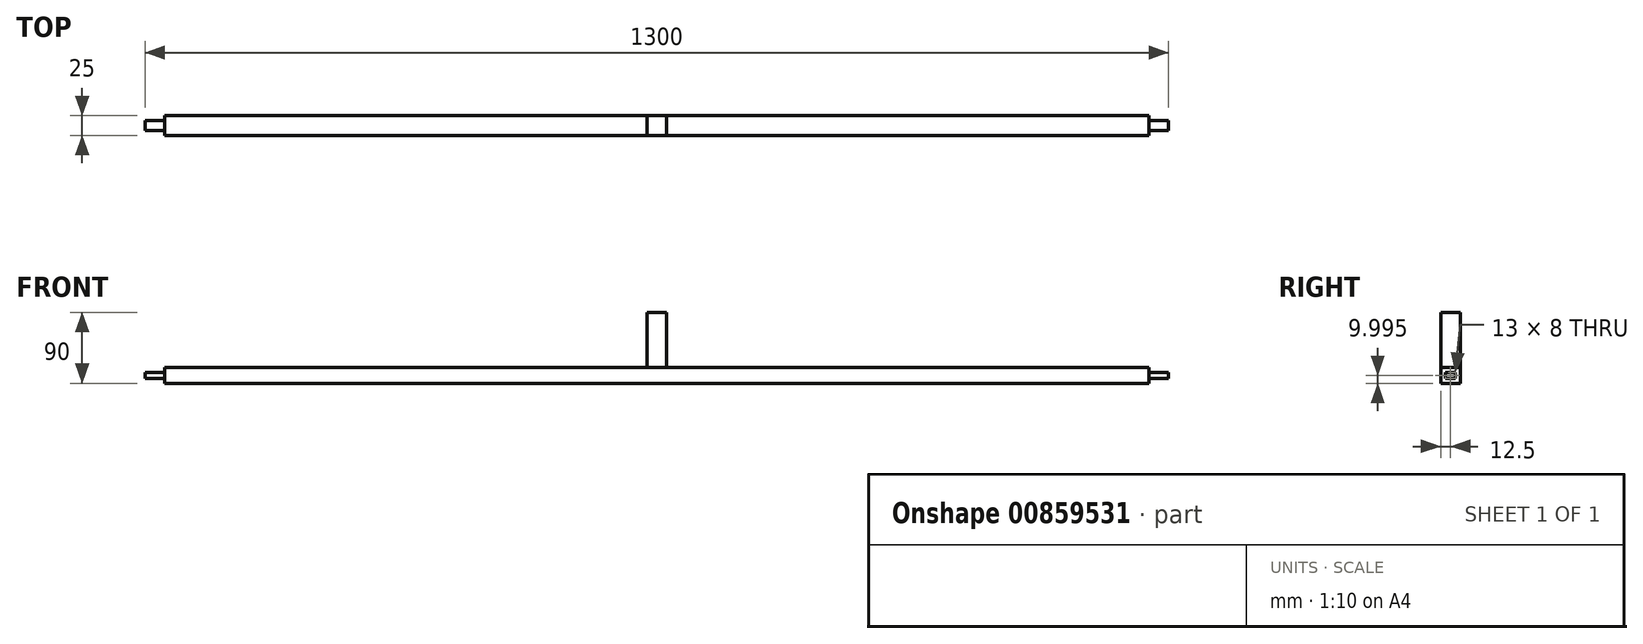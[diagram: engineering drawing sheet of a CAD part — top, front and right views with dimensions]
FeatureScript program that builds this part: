
annotation { "Feature Type Name" : "Feature", "Feature Type Description" : "" }
export const myFeature = defineFeature(function(context is Context, id is Id, definition is map)
    precondition{}
    {
        {
            var Q0;
            Q0=qCreatedBy(makeId("Right.planeOp"),FACE);
            var sketch = newSketch(context, id + "F0", { "sketchPlane" : qUnion([Q0])});
            skLineSegment(sketch, "E0.bottom", {"start": v(-29.86, 9.2) * mm, "end": v(-4.86, 9.2) * mm});
            skLineSegment(sketch, "E0.top", {"start": v(-29.86, -10.8) * mm, "end": v(-4.86, -10.8) * mm});
            skLineSegment(sketch, "E0.left", {"start": v(-29.86, 9.2) * mm, "end": v(-29.86, -10.8) * mm});
            skLineSegment(sketch, "E0.right", {"start": v(-4.86, 9.2) * mm, "end": v(-4.86, -10.8) * mm});
            skSolve(sketch);
        }
        {
            var Q0;
            Q0=makeQuery(id+"F0.imprint","IMPRINT",FACE,{"disambiguationData":[TD([[makeQuery(id+"F0.imprint","IMPRINT",EDGE,{"derivedFrom":sQuery(id+"F0.wireOp",EDGE,"E0.bottom")}),-1.0]])]});
            extrude(context, id + "F1", {"entities" : qUnion([Q0]), "depth" : (1250 / 2) * mm, "offsetDistance" : 25 * mm});
        }
        {
            var Q0;
            Q0=makeQuery(id+"F1.opExtrude","CAP_FACE",FACE,{"disambiguationData":[OSD([sQuery(id+"F0.wireOp",EDGE,"E0.bottom"),sQuery(id+"F0.wireOp",EDGE,"E0.top"),sQuery(id+"F0.wireOp",EDGE,"E0.left"),sQuery(id+"F0.wireOp",EDGE,"E0.right")])],"isStart":true});
            var sketch = newSketch(context, id + "F2", { "sketchPlane" : qUnion([Q0])});
            skLineSegment(sketch, "E1.bottom", {"start": v(10.86, 3.2) * mm, "end": v(23.86, 3.2) * mm});
            skLineSegment(sketch, "E1.top", {"start": v(10.86, -4.8) * mm, "end": v(23.86, -4.8) * mm});
            skLineSegment(sketch, "E1.left", {"start": v(10.86, 3.2) * mm, "end": v(10.86, -4.8) * mm});
            skLineSegment(sketch, "E1.right", {"start": v(23.86, 3.2) * mm, "end": v(23.86, -4.8) * mm});
            skSolve(sketch);
        }
        {
            var Q0;
            Q0=makeQuery(id+"F2.imprint","IMPRINT",FACE,{"disambiguationData":[TD([[makeQuery(id+"F2.imprint","IMPRINT",EDGE,{"derivedFrom":sQuery(id+"F2.wireOp",EDGE,"E1.bottom")}),-1.0]])]});
            extrude(context, id + "F3", {"entities" : qUnion([Q0]), "operationType" : NewBodyOperationType.ADD, "depth" : 25 * mm, "offsetDistance" : 25 * mm});
        }
        {
            var Q0;
            Q0=makeQuery(id+"F1.opExtrude","SWEPT_BODY",BODY,{"disambiguationData":[OSD([sQuery(id+"F0.wireOp",EDGE,"E0.bottom"),sQuery(id+"F0.wireOp",EDGE,"E0.top"),sQuery(id+"F0.wireOp",EDGE,"E0.left"),sQuery(id+"F0.wireOp",EDGE,"E0.right")])]});
            var Q1;
            Q1=makeQuery(id+"F1.opExtrude","CAP_FACE",FACE,{"disambiguationData":[OSD([sQuery(id+"F0.wireOp",EDGE,"E0.bottom"),sQuery(id+"F0.wireOp",EDGE,"E0.top"),sQuery(id+"F0.wireOp",EDGE,"E0.left"),sQuery(id+"F0.wireOp",EDGE,"E0.right")])],"isStart":false});
            mirror(context, id + "F4", {"operationType" : NewBodyOperationType.ADD, "entities" : qUnion([Q0]), "mirrorPlane" : qUnion([Q1])});
        }
        {
            var Q0;
            {var subQ0=makeQuery(id+"F1.opExtrude","SWEPT_FACE",FACE,{"disambiguationData":[OSD([sQuery(id+"F0.wireOp",EDGE,"E0.bottom")])]});Q0=makeQuery(id+"F4.boolean.opBoolean","MERGE",FACE,{"derivedFrom":[subQ0,makeQuery(id+"F4.opPattern","COPY",FACE,{"derivedFrom":subQ0,"instanceName":"1"})]});}
            var sketch = newSketch(context, id + "F5", { "sketchPlane" : qUnion([Q0])});
            skLineSegment(sketch, "E2", {"start": v(612.5, -4.86) * mm, "end": v(612.5, -29.86) * mm, "construction": true});
            skLineSegment(sketch, "E3.bottom", {"start": v(612.5, -4.86) * mm, "end": v(637.5, -4.86) * mm});
            skLineSegment(sketch, "E3.top", {"start": v(612.5, -29.86) * mm, "end": v(637.5, -29.86) * mm});
            skLineSegment(sketch, "E3.left", {"start": v(612.5, -4.86) * mm, "end": v(612.5, -29.86) * mm});
            skLineSegment(sketch, "E3.right", {"start": v(637.5, -4.86) * mm, "end": v(637.5, -29.86) * mm});
            skSolve(sketch);
        }
        {
            var Q0;
            Q0=makeQuery(id+"F5.imprint","IMPRINT",FACE,{"disambiguationData":[TD([[makeQuery(id+"F5.imprint","IMPRINT",EDGE,{"derivedFrom":sQuery(id+"F5.wireOp",EDGE,"E3.bottom")}),1.0]])]});
            extrude(context, id + "F6", {"entities" : qUnion([Q0]), "depth" : 70 * mm, "offsetDistance" : 25 * mm});
        }
    });
